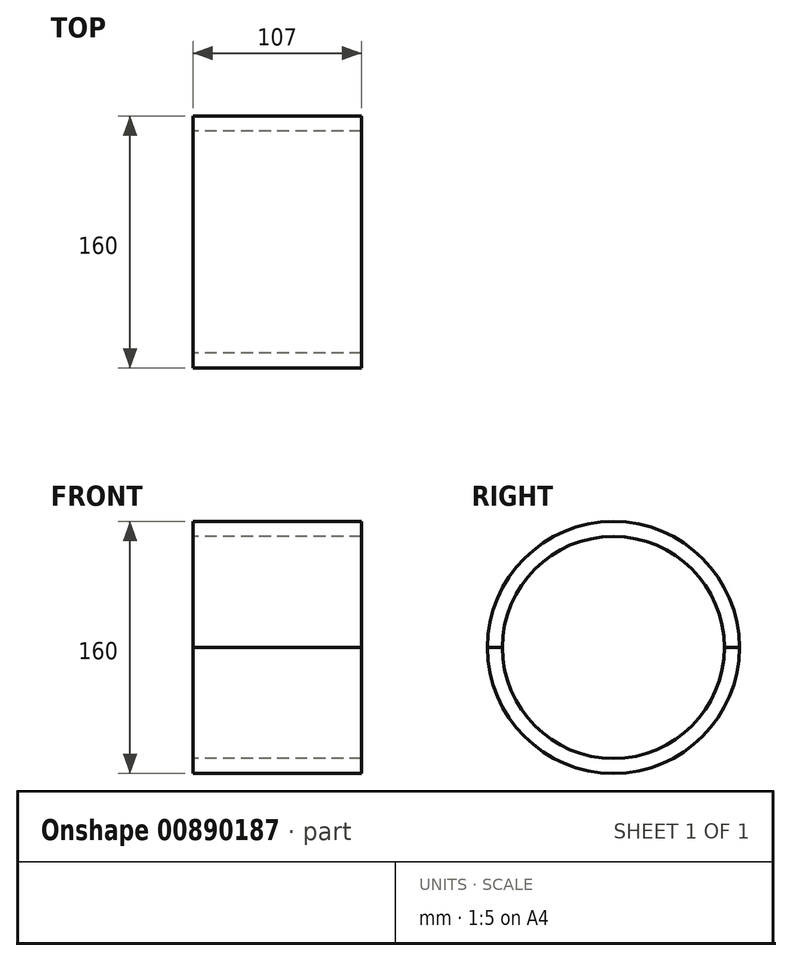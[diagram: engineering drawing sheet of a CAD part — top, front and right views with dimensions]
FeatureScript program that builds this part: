
annotation { "Feature Type Name" : "Feature", "Feature Type Description" : "" }
export const myFeature = defineFeature(function(context is Context, id is Id, definition is map)
    precondition{}
    {
        {
            var Q0;
            Q0=qCreatedBy(makeId("Front.planeOp"),FACE);
            var sketch = newSketch(context, id + "F0", { "sketchPlane" : qUnion([Q0])});
            skLineSegment(sketch, "E0.bottom", {"start": v(53.5, -80) * mm, "end": v(-53.5, -80) * mm});
            skLineSegment(sketch, "E0.top", {"start": v(53.5, 80) * mm, "end": v(-53.5, 80) * mm});
            skLineSegment(sketch, "E0.left", {"start": v(53.5, -80) * mm, "end": v(53.5, 80) * mm});
            skLineSegment(sketch, "E0.right", {"start": v(-53.5, -80) * mm, "end": v(-53.5, 80) * mm});
            skPoint(sketch, "E0.middle", {"position": v(0, 0) * mm});
            skLineSegment(sketch, "E1.bottom", {"start": v(53.5, -70.5) * mm, "end": v(-53.5, -70.5) * mm});
            skLineSegment(sketch, "E1.top", {"start": v(53.5, 70.5) * mm, "end": v(-53.5, 70.5) * mm});
            skLineSegment(sketch, "E1.left", {"start": v(53.5, -70.5) * mm, "end": v(53.5, 70.5) * mm});
            skLineSegment(sketch, "E1.right", {"start": v(-53.5, -70.5) * mm, "end": v(-53.5, 70.5) * mm});
            skLineSegment(sketch, "E2", {"start": v(0, 0) * mm, "end": v(200, 0) * mm, "construction": true});
            skSolve(sketch);
        }
        {
            var Q0;
            {var subQ0=sQuery(id+"F0.wireOp",EDGE,"E0.top");Q0=makeQuery(id+"F0.imprint","IMPRINT",FACE,{"disambiguationData":[TD([[makeQuery(id+"F0.imprint","IMPRINT",EDGE,{"derivedFrom":subQ0}),1.0]])]});}
            var Q1;
            {var subQ0=sQuery(id+"F0.wireOp",EDGE,"E0.bottom");Q1=makeQuery(id+"F0.imprint","IMPRINT",FACE,{"disambiguationData":[TD([[makeQuery(id+"F0.imprint","IMPRINT",EDGE,{"derivedFrom":subQ0}),-1.0]])]});}
            var Q2;
            Q2=sQuery(id+"F0.wireOp",EDGE,"E2");
            revolve(context, id + "F1", {"surfaceOperationType" : NewSurfaceOperationType.NEW, "entities" : qUnion([Q0, Q1]), "axis" : qUnion([Q2]), "revolveType" : RevolveType.SYMMETRIC, "angle" : 180 * degree});
        }
    });
